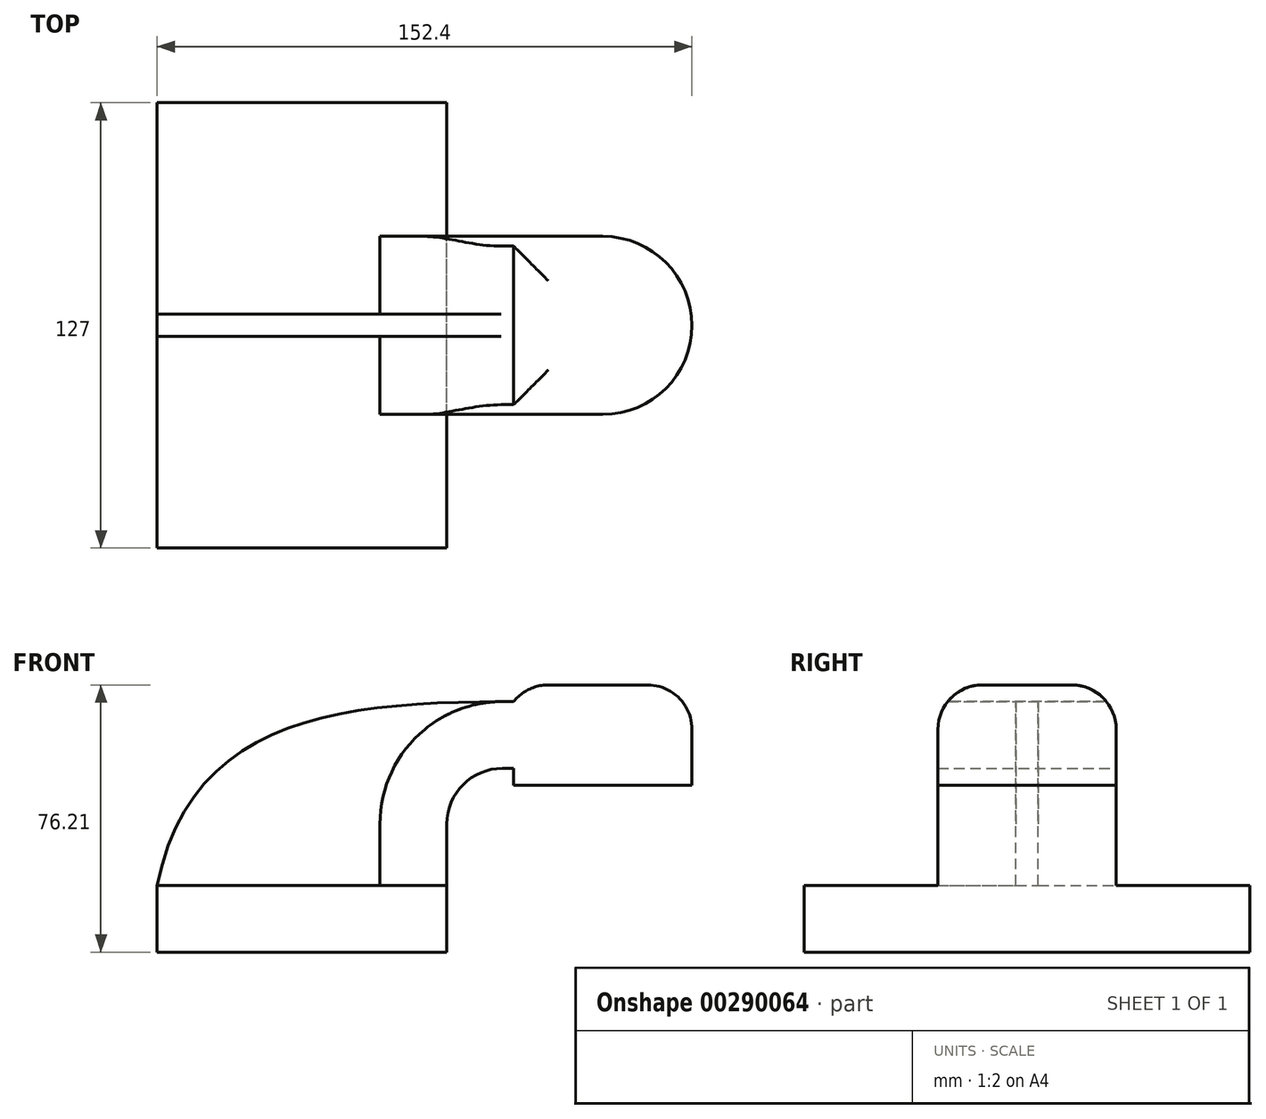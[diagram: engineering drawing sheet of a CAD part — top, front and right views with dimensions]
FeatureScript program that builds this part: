
annotation { "Feature Type Name" : "Feature", "Feature Type Description" : "" }
export const myFeature = defineFeature(function(context is Context, id is Id, definition is map)
    precondition{}
    {
        {
            var Q0;
            Q0=qCreatedBy(makeId("Front.planeOp"),FACE);
            var sketch = newSketch(context, id + "F0", { "sketchPlane" : qUnion([Q0])});
            skLineSegment(sketch, "E0.bottom", {"start": v(41.28, 9.53) * mm, "end": v(-41.28, 9.53) * mm});
            skLineSegment(sketch, "E0.top", {"start": v(41.28, -9.53) * mm, "end": v(-41.28, -9.53) * mm});
            skLineSegment(sketch, "E0.left", {"start": v(41.28, 9.53) * mm, "end": v(41.28, -9.53) * mm});
            skLineSegment(sketch, "E0.right", {"start": v(-41.28, 9.53) * mm, "end": v(-41.28, -9.53) * mm});
            skPoint(sketch, "E0.middle", {"position": v(0, 0) * mm});
            skLineSegment(sketch, "E1.bottom", {"start": v(111.12, 66.68) * mm, "end": v(60.32, 66.68) * mm});
            skLineSegment(sketch, "E1.top", {"start": v(111.12, 38.1) * mm, "end": v(60.32, 38.1) * mm});
            skLineSegment(sketch, "E1.left", {"start": v(111.12, 66.68) * mm, "end": v(111.12, 38.1) * mm});
            skLineSegment(sketch, "E1.right", {"start": v(60.32, 66.68) * mm, "end": v(60.32, 38.1) * mm});
            skPoint(sketch, "E1.middle", {"position": v(85.72, 52.39) * mm});
            skLineSegment(sketch, "E2", {"start": v(41.28, 9.53) * mm, "end": v(41.28, 27) * mm});
            skArc(sketch, "E3", {"start": v(41.28, 27) * mm, "mid": v(45.92, 38.23) * mm, "end": v(57.15, 42.88) * mm});
            skLineSegment(sketch, "E4", {"start": v(57.15, 42.88) * mm, "end": v(85.73, 42.88) * mm});
            skLineSegment(sketch, "E5.0", {"start": v(57.15, 61.93) * mm, "end": v(85.73, 61.93) * mm});
            skArc(sketch, "E5.1", {"start": v(22.23, 27) * mm, "mid": v(32.45, 51.7) * mm, "end": v(57.15, 61.93) * mm});
            skLineSegment(sketch, "E5.2", {"start": v(22.23, 9.53) * mm, "end": v(22.23, 27) * mm});
            skLineSegment(sketch, "E6", {"start": v(85.72, 38.1) * mm, "end": v(85.72, 66.68) * mm});
            skFitSpline(sketch, "E7", {"points": [v(-41.28, 9.52) * mm, v(57.15, 61.93) * mm], "startDerivative": vector(28.82, 142.58) * mm, "endDerivative": vector(142.48, 0.85) * mm});
            skSolve(sketch);
        }
        {
            var Q0;
            Q0=makeQuery(id+"F0.imprint","IMPRINT",FACE,{"disambiguationData":[TD([[makeQuery(id+"F0.imprint","IMPRINT",EDGE,{"derivedFrom":sQuery(id+"F0.wireOp",EDGE,"E0.top")}),-1.0]])]});
            extrude(context, id + "F1", {"entities" : qUnion([Q0]), "endBound" : BoundingType.SYMMETRIC, "depth" : 127 * mm});
        }
        {
            var Q0;
            {var subQ1=sQuery(id+"F0.wireOp",EDGE,"E2");Q0=makeQuery(id+"F0.imprint","IMPRINT",FACE,{"disambiguationData":[TD([[makeQuery(id+"F0.imprint","IMPRINT",EDGE,{"derivedFrom":subQ1}),1.0]])]});}
            var Q1;
            {var subQ0=sQuery(id+"F0.wireOp",EDGE,"E5.0");var subQ1=sQuery(id+"F0.wireOp",EDGE,"E1.right");var subQ2=makeQuery(id+"F0.imprint","INTERSECT",VERTEX,{"derivedFrom":[subQ1,subQ0]});Q1=makeQuery(id+"F0.imprint","IMPRINT",FACE,{"disambiguationData":[TD([[makeQuery(id+"F0.imprint","IMPRINT",EDGE,{"disambiguationData":[TD([[subQ2,-1.0]])],"derivedFrom":subQ1}),1.0]])]});}
            var Q2;
            {var subQ0=sQuery(id+"F0.wireOp",EDGE,"E1.right");var subQ1=sQuery(id+"F0.wireOp",EDGE,"E1.bottom");var subQ2=makeQuery(id+"F0.imprint","INTERSECT",VERTEX,{"derivedFrom":[subQ1,subQ0]});Q2=makeQuery(id+"F0.imprint","IMPRINT",FACE,{"disambiguationData":[TD([[makeQuery(id+"F0.imprint","IMPRINT",EDGE,{"disambiguationData":[TD([[subQ2,1.0]])],"derivedFrom":subQ1}),1.0]])]});}
            var Q3;
            {var subQ0=sQuery(id+"F0.wireOp",EDGE,"E1.right");var subQ1=sQuery(id+"F0.wireOp",EDGE,"E1.top");var subQ2=makeQuery(id+"F0.imprint","INTERSECT",VERTEX,{"derivedFrom":[subQ1,subQ0]});Q3=makeQuery(id+"F0.imprint","IMPRINT",FACE,{"disambiguationData":[TD([[makeQuery(id+"F0.imprint","IMPRINT",EDGE,{"disambiguationData":[TD([[subQ2,1.0]])],"derivedFrom":subQ1}),-1.0]])]});}
            extrude(context, id + "F2", {"entities" : qUnion([Q0, Q1, Q2, Q3]), "operationType" : NewBodyOperationType.ADD, "endBound" : BoundingType.SYMMETRIC, "depth" : 50.8 * mm});
        }
        {
            var Q0;
            {var subQ0=sQuery(id+"F0.wireOp",EDGE,"E1.left");Q0=makeQuery(id+"F0.imprint","IMPRINT",FACE,{"disambiguationData":[TD([[makeQuery(id+"F0.imprint","IMPRINT",EDGE,{"derivedFrom":subQ0}),-1.0]])]});}
            var Q1;
            Q1=sQuery(id+"F0.wireOp",EDGE,"E6");
            revolve(context, id + "F3", {"operationType" : NewBodyOperationType.ADD, "entities" : qUnion([Q0]), "axis" : qUnion([Q1]), "revolveType" : RevolveType.FULL});
        }
        {
            var Q0;
            {var subQ3=sQuery(id+"F0.wireOp",EDGE,"E5.2");Q0=makeQuery(id+"F0.imprint","IMPRINT",FACE,{"disambiguationData":[TD([[makeQuery(id+"F0.imprint","IMPRINT",EDGE,{"derivedFrom":subQ3}),1.0]])]});}
            extrude(context, id + "F4", {"entities" : qUnion([Q0]), "operationType" : NewBodyOperationType.ADD, "endBound" : BoundingType.SYMMETRIC, "depth" : 6.35 * mm});
        }
        {
            var Q0;
            {var subQ0=sQuery(id+"F0.wireOp",EDGE,"E1.bottom");Q0=makeQuery(id+"F3.boolean.opBoolean","MERGE",FACE,{"derivedFrom":[makeQuery(id+"F2.opExtrude","SWEPT_FACE",FACE,{"disambiguationData":[OSD([subQ0])]}),makeQuery(id+"F3.opRevolve","SWEPT_FACE",FACE,{"disambiguationData":[OSD([subQ0])]})]});}
            fillet(context, id + "F5", {"entities" : qUnion([Q0]), "radius" : 12.7 * mm, "tangentPropagation" : true, "allowEdgeOverflow" : false});
        }
    });
